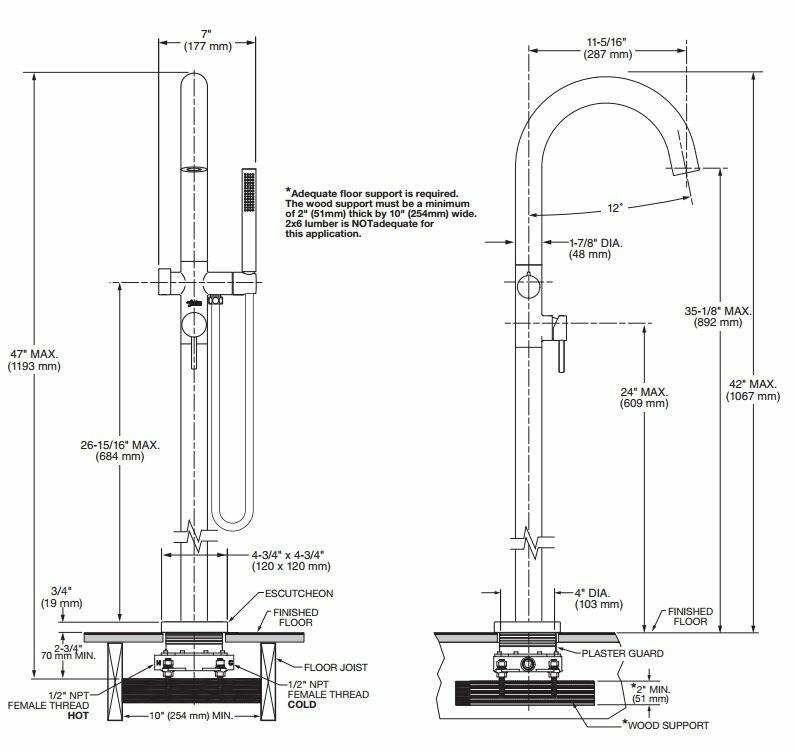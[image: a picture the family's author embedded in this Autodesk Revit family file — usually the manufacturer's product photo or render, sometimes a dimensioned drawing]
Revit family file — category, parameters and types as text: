
# Revit family: Bathtub-Freestanding-American_Standard-Cadet-2764.014M202.011
name_source: partatom
category: Plumbing Fixtures
revit_build: Autodesk Revit 2018 (Build: 20170223_1515(x64)
units: mm (PartAtom-declared; Revit-internal decimal feet)

## family parameters
Always vertical = No
Cut with Voids When Loaded = No
OmniClass Number = 23.45.05.14.21
OmniClass Title = Bathtubs
Part Type = Normal
Room Calculation Point = No
Round Connector Dimension = Use Diameter
Shared = Yes
Work Plane-Based = Yes

## types (4) — shared parameters
1583.470-Universal Bathtub Drain = No
1640.305-Deep Soak Bathtub Drain = No
Assembly Code = D2010510
CW Connection = Yes
CWFU = 3
Default Elevation = 0"
Drain / Overflow Cover = Yes
Drain Size = 2 1/8"
Finish = Acrylic-American Standard-011-Arctic
HW Connection = Yes
HWFU = 3
Height = 23"
IAPMO Compliance = Meets or Exceeds the Following Specifications:• CSA B45.5 / IAPMO Z124
Installation Type = Floor Mounted
Length = 66"
Manufacturer = American Standard
Material = Acrylic-American Standard-011-Arctic
Price = Prices may vary. Please consult Manufacturer Representative for most up-to-date price list.
Product Documentation Link = https://americanstandard.box.com
Product Page URL = https://www.americanstandard-us.com
Revised Date = 05/16/2022
Shipping Weight = 120 Lbs. (54 Kg.)
Tub Filler Height = 43 1/8"
URL = https://www.americanstandard-us.com
Vent Connection = No
WFU = 4
Warranty Information = Limited Lifetime warranty
Waste Connection = Yes
Waste Connection Diameter = 1"
Width = 32"

## per-type parameters (varying)
| type | Description | Drain and Tub Filler Material | Inlet Connection Diameter | Tub Filler - Freestanding tub filler with hand spray |
| 2764014M202 | Cadet® 66 x 32-Inch Freestanding Bathtub With Polished Chrome Finish Filler and Drain Kit | Metal-American Standard-002-Polished Chrome | 3/4" | Yes |
| 2764.014 | Cadet® 66 x 32-Inch Freestanding Bathtub With Drain Chrome Finish | Metal-American Standard-002-Polished Chrome | 0" | No |
| 2764.014M203 | Cadet® 66 x 32-Inch Freestanding Bathtub With Brushed Nickel Finish Filler and Drain Kit | Metal-American Standard-Brushed Nickel | 3/4" | Yes |
| 2764.014M204 | Cadet® 66 x 32-Inch Freestanding Bathtub With Drain Brushed Nickel Finish | Metal-American Standard-Brushed Nickel | 0" | No |

note: column(s) folded — value = type name in every type: Model

## geometry (parser evidence)
native form markers: Sweep x5
no freeform markers — native parametric forms only
